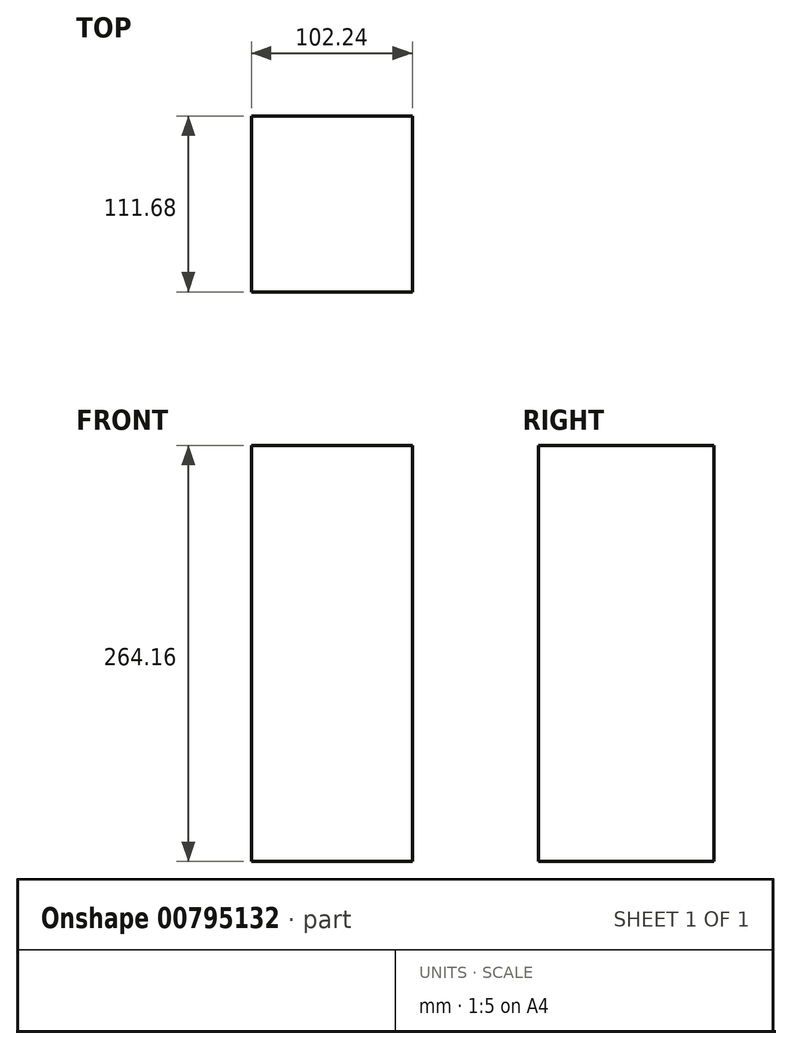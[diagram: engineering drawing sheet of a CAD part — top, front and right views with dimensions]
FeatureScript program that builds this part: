
annotation { "Feature Type Name" : "Feature", "Feature Type Description" : "" }
export const myFeature = defineFeature(function(context is Context, id is Id, definition is map)
    precondition{}
    {
        {
            var Q0;
            Q0=qCreatedBy(makeId("Top.planeOp"),FACE);
            var sketch = newSketch(context, id + "F0", { "sketchPlane" : qUnion([Q0])});
            skLineSegment(sketch, "E0.bottom", {"start": v(-51.12, 55.84) * mm, "end": v(51.12, 55.84) * mm});
            skLineSegment(sketch, "E0.top", {"start": v(-51.12, -55.84) * mm, "end": v(51.12, -55.84) * mm});
            skLineSegment(sketch, "E0.left", {"start": v(-51.12, 55.84) * mm, "end": v(-51.12, -55.84) * mm});
            skLineSegment(sketch, "E0.right", {"start": v(51.12, 55.84) * mm, "end": v(51.12, -55.84) * mm});
            skPoint(sketch, "E0.middle", {"position": v(0, 0) * mm});
            skSolve(sketch);
        }
        {
            var Q0;
            Q0=makeQuery(id+"F0.imprint","IMPRINT",FACE,{"disambiguationData":[TD([[makeQuery(id+"F0.imprint","IMPRINT",EDGE,{"derivedFrom":sQuery(id+"F0.wireOp",EDGE,"E0.bottom")}),-1.0]])]});
            extrude(context, id + "F1", {"entities" : qUnion([Q0]), "depth" : 264.16 * mm, "offsetDistance" : 25.4 * mm});
        }
    });
